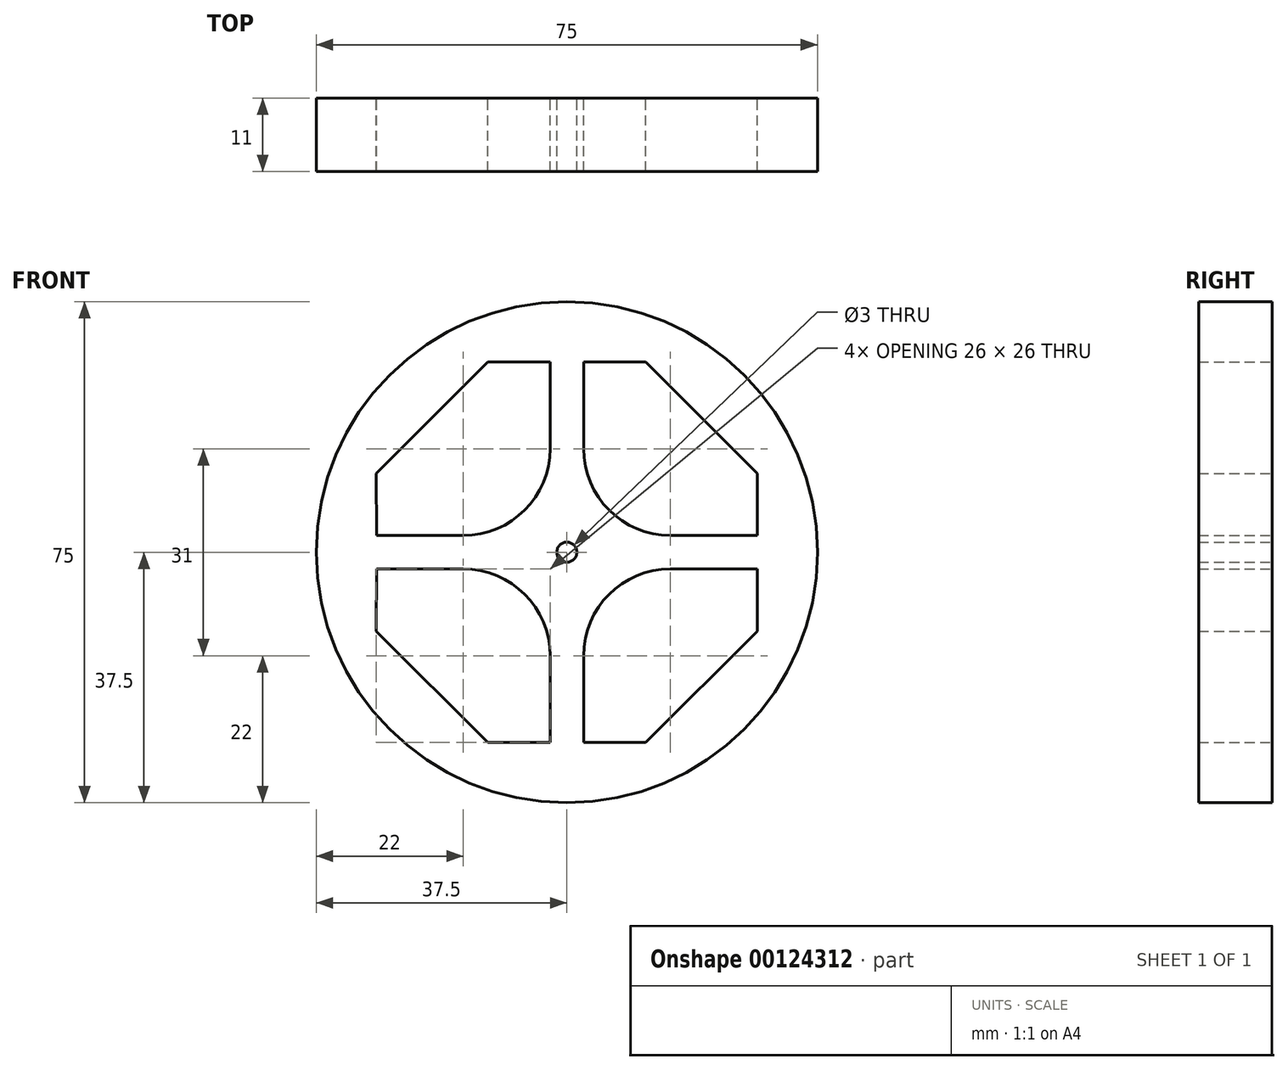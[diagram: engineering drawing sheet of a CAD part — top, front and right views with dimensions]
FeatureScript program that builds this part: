
annotation { "Feature Type Name" : "Feature", "Feature Type Description" : "" }
export const myFeature = defineFeature(function(context is Context, id is Id, definition is map)
    precondition{}
    {
        {
            var Q0;
            Q0=qCreatedBy(makeId("Front.planeOp"),FACE);
            var sketch = newSketch(context, id + "F0", { "sketchPlane" : qUnion([Q0])});
            skCircle(sketch, "E0", {"center": v(0, 0) * mm, "radius": 37.5 * mm});
            skArc(sketch, "E1", {"start": v(-15.5, 2.5) * mm, "mid": v(-6.3, 6.3) * mm, "end": v(-2.5, 15.5) * mm});
            skPoint(sketch, "E1.centerSnap0", {"position": v(-15.5, 2.5) * mm});
            skPoint(sketch, "E1.centerSnap1", {"position": v(-2.5, 15.5) * mm});
            skArc(sketch, "E2", {"start": v(15.5, 2.5) * mm, "mid": v(6.3, 6.3) * mm, "end": v(2.5, 15.5) * mm});
            skPoint(sketch, "E2.centerSnap0", {"position": v(15.5, 2.5) * mm});
            skArc(sketch, "E3", {"start": v(15.5, -2.5) * mm, "mid": v(6.3, -6.3) * mm, "end": v(2.5, -15.5) * mm});
            skPoint(sketch, "E3.centerSnap0", {"position": v(2.5, -15.5) * mm});
            skPoint(sketch, "E3.centerSnap1", {"position": v(15.5, -2.5) * mm});
            skArc(sketch, "E4", {"start": v(-15.5, -2.5) * mm, "mid": v(-6.3, -6.3) * mm, "end": v(-2.5, -15.5) * mm});
            skPoint(sketch, "E4.centerSnap0", {"position": v(-2.5, -15.5) * mm});
            skPoint(sketch, "E4.centerSnap1", {"position": v(-15.5, -2.5) * mm});
            skLineSegment(sketch, "E5", {"start": v(-11.8, 28.5) * mm, "end": v(-28.5, 11.8) * mm});
            skLineSegment(sketch, "E6", {"start": v(11.8, 28.5) * mm, "end": v(28.5, 11.8) * mm});
            skLineSegment(sketch, "E7", {"start": v(28.5, -11.8) * mm, "end": v(11.8, -28.5) * mm});
            skLineSegment(sketch, "E8", {"start": v(-11.8, -28.5) * mm, "end": v(-28.5, -11.8) * mm});
            skLineSegment(sketch, "E9", {"start": v(-28.5, 11.8) * mm, "end": v(-28.47, 2.5) * mm});
            skLineSegment(sketch, "E10", {"start": v(-11.8, 28.5) * mm, "end": v(-2.5, 28.5) * mm});
            skLineSegment(sketch, "E11", {"start": v(2.5, 28.5) * mm, "end": v(11.8, 28.5) * mm});
            skLineSegment(sketch, "E12", {"start": v(28.5, 11.8) * mm, "end": v(28.5, 2.5) * mm});
            skLineSegment(sketch, "E13", {"start": v(28.5, -2.5) * mm, "end": v(28.5, -11.8) * mm});
            skLineSegment(sketch, "E14", {"start": v(2.5, -28.5) * mm, "end": v(11.8, -28.5) * mm});
            skLineSegment(sketch, "E15", {"start": v(-2.5, -28.5) * mm, "end": v(-11.8, -28.5) * mm});
            skLineSegment(sketch, "E16", {"start": v(-28.5, -11.8) * mm, "end": v(-28.47, -2.5) * mm});
            skLineSegment(sketch, "E17", {"start": v(-2.5, 28.5) * mm, "end": v(-2.5, 15.5) * mm});
            skLineSegment(sketch, "E18", {"start": v(-28.47, 2.5) * mm, "end": v(-15.5, 2.5) * mm});
            skLineSegment(sketch, "E19", {"start": v(-28.47, -2.5) * mm, "end": v(-15.5, -2.5) * mm});
            skLineSegment(sketch, "E20", {"start": v(-2.5, -15.5) * mm, "end": v(-2.5, -28.5) * mm});
            skLineSegment(sketch, "E21", {"start": v(2.5, -28.5) * mm, "end": v(2.5, -15.5) * mm});
            skLineSegment(sketch, "E22", {"start": v(15.5, -2.5) * mm, "end": v(28.5, -2.5) * mm});
            skLineSegment(sketch, "E23", {"start": v(28.5, 2.5) * mm, "end": v(15.5, 2.5) * mm});
            skLineSegment(sketch, "E24", {"start": v(2.5, 15.5) * mm, "end": v(2.5, 28.5) * mm});
            skCircle(sketch, "E25", {"center": v(0, 0) * mm, "radius": 1.5 * mm});
            skSolve(sketch);
        }
        {
            var Q0;
            Q0=makeQuery(id+"F0.imprint","IMPRINT",FACE,{"disambiguationData":[TD([[makeQuery(id+"F0.imprint","IMPRINT",EDGE,{"derivedFrom":sQuery(id+"F0.wireOp",EDGE,"E0")}),1.0]])]});
            extrude(context, id + "F1", {"entities" : qUnion([Q0]), "depth" : 11 * mm});
        }
    });
